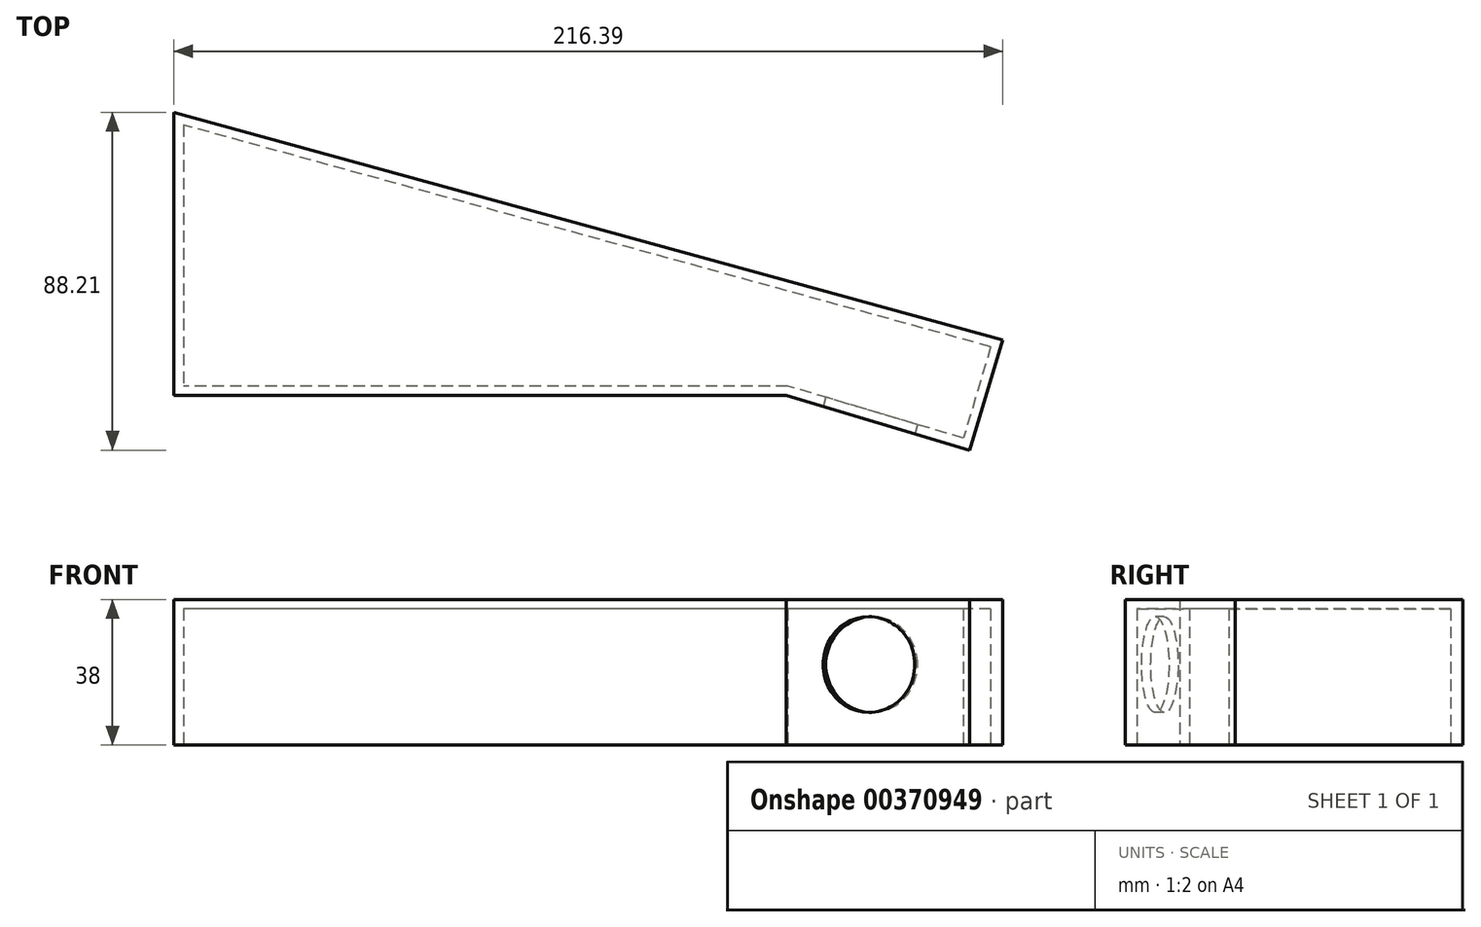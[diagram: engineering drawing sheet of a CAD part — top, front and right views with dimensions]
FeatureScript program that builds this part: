
annotation { "Feature Type Name" : "Feature", "Feature Type Description" : "" }
export const myFeature = defineFeature(function(context is Context, id is Id, definition is map)
    precondition{}
    {
        {
            var Q0;
            Q0=qCreatedBy(makeId("Top.planeOp"),FACE);
            var sketch = newSketch(context, id + "F0", { "sketchPlane" : qUnion([Q0])});
            skLineSegment(sketch, "E0.bottom", {"start": v(159.91, -43.94) * mm, "end": v(0, 0) * mm});
            skLineSegment(sketch, "E0.top", {"start": v(159.91, -73.94) * mm, "end": v(0, -73.94) * mm});
            skLineSegment(sketch, "E0.left", {"start": v(0, 0) * mm, "end": v(0, -73.94) * mm});
            skLineSegment(sketch, "E1", {"start": v(159.91, -43.94) * mm, "end": v(216.4, -59.46) * mm});
            skLineSegment(sketch, "E2", {"start": v(216.4, -59.46) * mm, "end": v(207.83, -88.21) * mm});
            skLineSegment(sketch, "E3", {"start": v(207.83, -88.21) * mm, "end": v(159.91, -73.94) * mm});
            skPoint(sketch, "E4", {"position": v(188, -67.21) * mm});
            skSolve(sketch);
        }
        {
            var Q0;
            Q0 = qSketchRegion(id + "F0", true);
            extrude(context, id + "F1", {"entities" : qUnion([Q0]), "depth" : 38 * mm});
        }
        {
            var Q0;
            Q0=makeQuery(id+"F1.opExtrude","CAP_FACE",FACE,{"disambiguationData":[OSD([sQuery(id+"F0.wireOp",EDGE,"E0.bottom"),sQuery(id+"F0.wireOp",EDGE,"E0.top"),sQuery(id+"F0.wireOp",EDGE,"E0.left"),sQuery(id+"F0.wireOp",EDGE,"E1"),sQuery(id+"F0.wireOp",EDGE,"E2"),sQuery(id+"F0.wireOp",EDGE,"E3")])],"isStart":true});
            shell(context, id + "F2", {"entities" : qUnion([Q0]), "thickness" : 2.5 * mm});
        }
        {
            var Q0;
            Q0=makeQuery(id+"F1.opExtrude","SWEPT_FACE",FACE,{"disambiguationData":[OSD([sQuery(id+"F0.wireOp",EDGE,"E3")])]});
            var sketch = newSketch(context, id + "F3", { "sketchPlane" : qUnion([Q0])});
            skCircle(sketch, "E5", {"center": v(196.86, 21) * mm, "radius": 12.5 * mm});
            skSolve(sketch);
        }
        {
            var Q0;
            Q0 = qSketchRegion(id + "F3", true);
            extrude(context, id + "F4", {"entities" : qUnion([Q0]), "operationType" : NewBodyOperationType.REMOVE, "oppositeDirection" : true, "depth" : 5 * mm});
        }
    });
